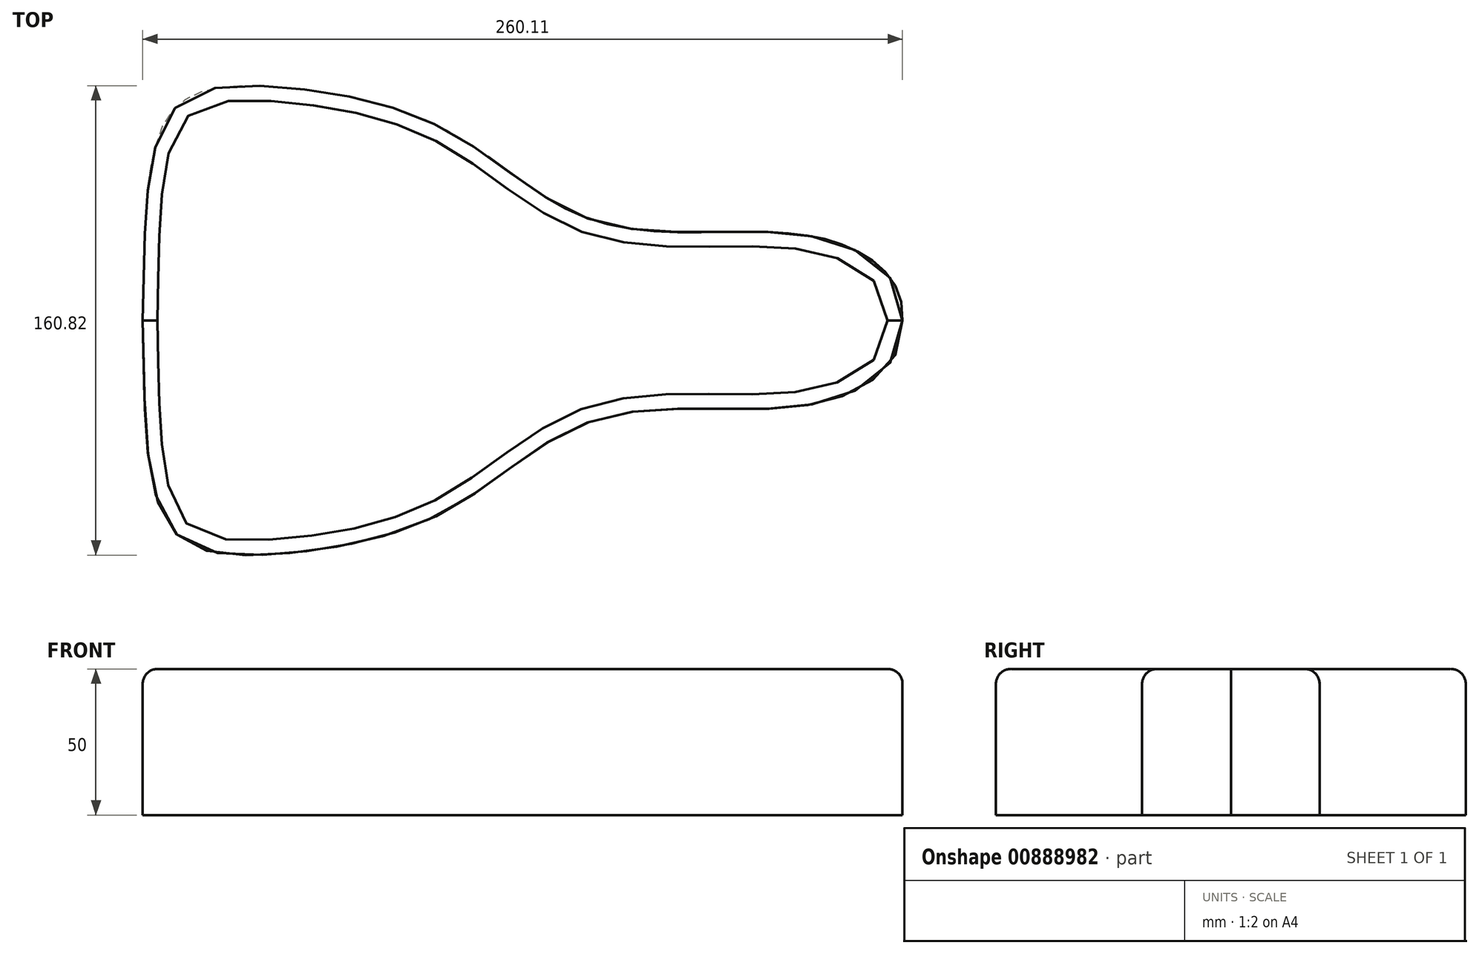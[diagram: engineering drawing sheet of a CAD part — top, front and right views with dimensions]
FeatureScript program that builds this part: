
annotation { "Feature Type Name" : "Feature", "Feature Type Description" : "" }
export const myFeature = defineFeature(function(context is Context, id is Id, definition is map)
    precondition{}
    {
        {
            var Q0;
            Q0=qCreatedBy(makeId("Top.planeOp"),FACE);
            var sketch = newSketch(context, id + "F0", { "sketchPlane" : qUnion([Q0])});
            skLineSegment(sketch, "E0", {"start": v(0, 0) * mm, "end": v(260, 0) * mm});
            skFitSpline(sketch, "E1", {"points": [v(0, 0) * mm, v(10.12, -71.66) * mm, v(45.56, -80) * mm, v(103.7, -65.36) * mm, v(152.15, -35) * mm, v(208.3, -30.37) * mm, v(244.48, -23.76) * mm, v(260, 0) * mm], "startDerivative": vector(15.8, -505.37) * mm, "endDerivative": vector(-30.64, 314.77) * mm});
            skFitSpline(sketch, "E2.MirrorCS", {"points": [v(0, 0) * mm, v(10.12, 71.66) * mm, v(45.56, 80) * mm, v(103.7, 65.36) * mm, v(152.15, 35) * mm, v(208.3, 30.37) * mm, v(244.48, 23.76) * mm, v(260, 0) * mm], "startDerivative": vector(15.8, 505.37) * mm, "endDerivative": vector(-30.64, -314.77) * mm});
            skSolve(sketch);
        }
        {
            var Q0;
            Q0=qSketchRegion(id+"F0",true);
            var Q1;
            Q1=makeQuery(id+"F0.imprint","IMPRINT",FACE,{"disambiguationData":[TD([[makeQuery(id+"F0.imprint","IMPRINT",EDGE,{"derivedFrom":sQuery(id+"F0.wireOp",EDGE,"E0")}),-1.0]])]});
            extrude(context, id + "F1", {"entities" : qUnion([Q0, Q1]), "depth" : 50 * mm, "offsetDistance" : 25 * mm});
        }
        {
            var Q0;
            Q0=makeQuery(id+"F1.opExtrude","CAP_FACE",FACE,{"disambiguationData":[OSD([sQuery(id+"F0.wireOp",EDGE,"E1"),sQuery(id+"F0.wireOp",EDGE,"E2.MirrorCS")])],"isStart":false});
            fillet(context, id + "F2", {"entities" : qUnion([Q0]), "radius" : 5 * mm, "tangentPropagation" : true, "allowEdgeOverflow" : false});
        }
    });
